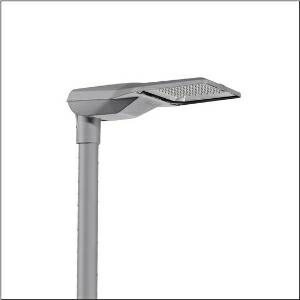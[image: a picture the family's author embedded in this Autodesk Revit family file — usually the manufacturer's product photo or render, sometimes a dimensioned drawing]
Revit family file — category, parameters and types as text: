
# Revit family: streetlight_sl_21_iq_midi___st1_0a_5xe3d31g08nb_2a13
name_source: partatom
category: Lighting Fixtures
units: mm (PartAtom-declared; Revit-internal decimal feet)

## family parameters
Cut with Voids When Loaded = No
Host = Face
Light Source = No
Part Type = Normal
Room Calculation Point = No
Round Connector Dimension = Use Diameter
Shared = No

## types (1)
- --- (1 x LED, 23230 lm, 155.5 W, 3000K)
    Apparent Load = 155 VA
    CIE Flux Codes = 40 73 97 100 100
    Color Rendering = 70
    Color Temperature = 3000K
    Default Elevation = 1800 mm
    Description = Streetlight SL 21 iQ midi, mast luminaire, primary light control with lens, of PMMA, primary optical cover: cover, of toughened safety glass, transparent, light distribution: ST1.0a, light emission: direct distribution, primary light characteristic: asymmetric, installation type: post-top, side-entry, LED, High Power LED, rated luminous flux: 23.230lm, luminous efficacy: 149lm/W, light colour: 730, colour temperature: 3000K, control gear: iQ Street-Remote, control: Street-Remote, Auto-Match, Temp-Guard, Lumen-Switch, Night-Set, Smart-Wire, Light-Fading, Desk-Remote (wireless, voltage-free reading and setting of iQ features in the workshop via application-optimized NFC function/RFID function), optimised constant luminous flux control (CLO 2.0), pre-setting: linear dimming characteristic, mains connection: 230..240V, AC, 50/60Hz, start of lifetime: 156W, end of service life: 162W, reduction: 69W, luminaire housing, of diecast aluminium, powder-coated, SITECO metallic grey (DB 702S), corrosivity category C5 high according to DIN EN ISO 12944, please order mast flange separately, inclination adjustable: 0°, 5°, 10°, 15°, sealing non-destructively replaceable, multi-level sealing system, length: 644mm, width: 335mm, height: 110mm, mast flange for spigot size: 42mm (side-entry): 5XC10008XM4, 60/48mm (side-entry/post-top): 5XC10108XM2, 76/60mm (side-entry/post-top): 5XC10108XM1, mounting height: 4..8m, protection rating (complete): IP66, insulation class (complete): insulation class II (safety insulation), certification: CE, ENEC, ENEC+, VDE, impact resistance: IK10, permissible operating ambient temperature for outdoor applications: -40..+50°C, standard-compliant lighting for roads and squares, packaging unit: 1 piece

Light Distribution: ST1.0a
    Height = 111 mm
    Lamp = 1 x LED
    Lamp Light Flux = 23230 lm
    Lamp Power = 155.5 W
    Lamp count = 1
    Length = 644 mm
    Luminous efficacy = 149 lm/W
    Manufacturer = Siteco
    ModVariant = No
    Model = 5XE3D31G08NB
    Number of Poles = 1
    OnlyDefault = Yes
    Power Factor = 1
    Product Name = Streetlight SL 21 iQ midi | ST1.0a
    Product group = mast luminaire | pylon top
    ProductGroupID = 6100
    Protection Class = Protection class II
    Protection Degree = IP 66
    RLX_Detail_Level = 1
    RLX_Emergency_Light_Flux = 0 lm
    RLX_Emergency_Type = 0
    RLX_Emergency_Type_DB = No
    RlxData = <blob elided: 27249 chars, md5=010d9da0>
    Socket = socket
    Standby Power = 0 W
    System Light Flux = 23230 lm
    System Power = 155 W
    Type Comments = factory setting: luminous flux: 100 % | dim-lin: 254 | 823 mA
    Type Image = l_1004298.jpg
    URL = http://relux.com
    VarID = @adj_170327
    Voltage = 0 V
    Weight = 0.00 kg
    Width = 336 mm

## geometry (parser evidence)
native form markers: Blend x4, Sweep x11
no freeform markers — native parametric forms only
